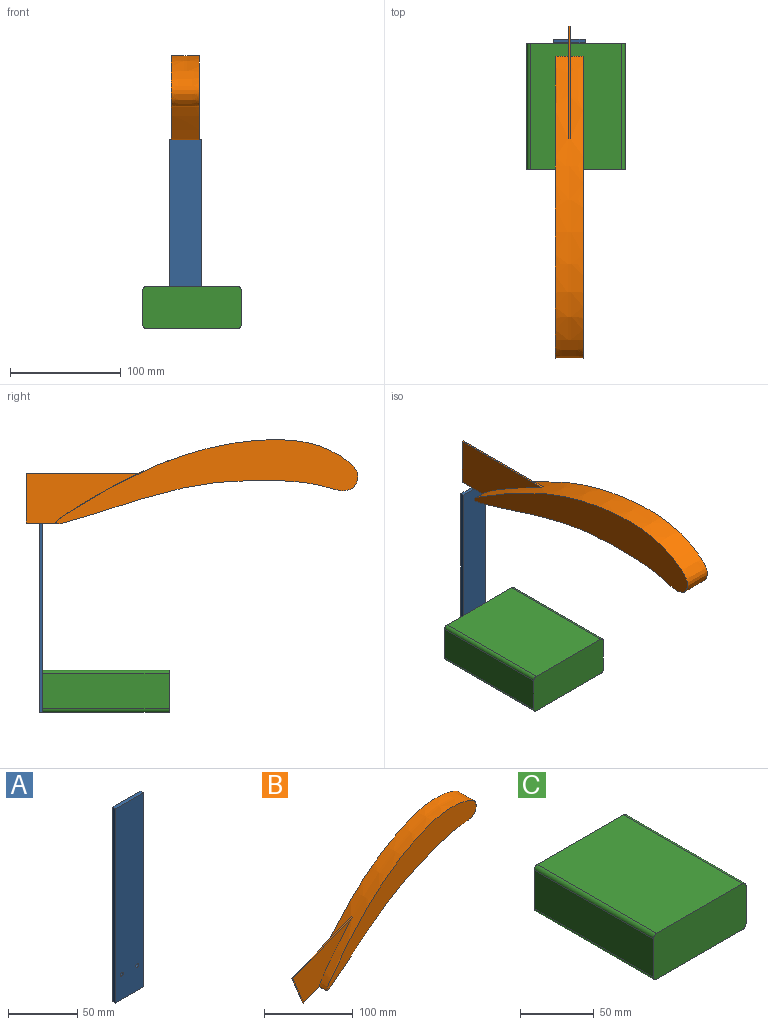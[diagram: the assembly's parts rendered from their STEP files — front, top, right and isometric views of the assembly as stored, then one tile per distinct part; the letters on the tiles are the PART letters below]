
ASSEMBLY  parts=3 mates=3
PART A: 8 faces, bbox 28.6x3.2x171.5 mm
  f0: plane 171.45x3.18mm, normal (1,0,0), area 544.4mm2, adj f1,f4,f6,f7
  f1: plane 28.58x3.18mm, normal (0,0,1), area 90.7mm2, adj f0,f2,f6,f7
  f2: plane 171.45x3.18mm, normal (-1,0,0), area 544.4mm2, adj f1,f4,f6,f7
  f3: cylinder r=1.59mm len=3.18mm, axis (0,-1,0), area 31.7mm2, adj f6,f7
  f4: plane 28.58x3.18mm, normal (0,0,-1), area 90.7mm2, adj f0,f2,f6,f7
  f5: cylinder r=1.59mm len=3.18mm, axis (0,-1,0), area 31.7mm2, adj f6,f7
  f6: plane 171.45x28.58mm, normal (0,1,0), area 4883.3mm2, adj f0,f1,f2,f3,f4,f5
  f7: plane 171.45x28.58mm, normal (0,-1,0), area 4883.3mm2, adj f0,f1,f2,f3,f4,f5
PART B: 8 faces, bbox 281x25.4x166.1 mm
  f0: extruded ~237.77x154.23mm, area 14786.6mm2, adj f1,f2,f3,f5,f6,f7
  f1: plane 241.53x156.81mm, normal (0,-1,0), area 7523.9mm2, adj f0
  f2: plane 241.53x156.81mm, normal (0,1,0), area 7523.9mm2, adj f0
  f3: plane 94.57x38.21mm, normal (-0.37,0,0.93), area 161.9mm2, adj f0,f4,f6,f7
  f4: plane 41.72x16.86mm, normal (-0.93,0,-0.37), area 71.4mm2, adj f3,f5,f6,f7
  f5: plane 25.19x10.18mm, normal (0.37,0,-0.93), area 43.1mm2, adj f0,f4,f6,f7
  f6: plane 96.16x81.52mm, normal (0,-1,0), area 2729.3mm2, adj f0,f3,f4,f5
  f7: plane 96.16x81.52mm, normal (0,1,0), area 2729.3mm2, adj f0,f3,f4,f5
PART C: 10 faces, bbox 88.9x114.3x38.1 mm
  f0: plane 114.3x31.75mm, normal (-1,0,0), area 3629mm2, adj f1,f7,f8,f9
  f1: cylinder r=3.17mm len=114.3mm, axis (0,1,0), area 570mm2, adj f0,f2,f8,f9
  f2: plane 114.3x82.55mm, normal (0,0,-1), area 9435.5mm2, adj f1,f3,f8,f9
  f3: cylinder r=3.17mm len=114.3mm, axis (0,1,0), area 570mm2, adj f2,f4,f8,f9
  f4: plane 114.3x31.75mm, normal (1,0,0), area 3629mm2, adj f3,f5,f8,f9
  f5: cylinder r=3.17mm len=114.3mm, axis (0,1,0), area 570mm2, adj f4,f6,f8,f9
  f6: plane 114.3x82.55mm, normal (0,0,1), area 9435.5mm2, adj f5,f7,f8,f9
  f7: cylinder r=3.17mm len=114.3mm, axis (0,1,0), area 570mm2, adj f0,f6,f8,f9
  f8: plane 88.9x38.1mm, normal (0,-1,0), area 3378.4mm2, adj f0,f1,f2,f3,f4,f5,f6,f7
  f9: plane 88.9x38.1mm, normal (0,1,0), area 3378.4mm2, adj f0,f1,f2,f3,f4,f5,f6,f7
PLACE A t=(-47.32,20.64,82.55)mm
PLACE B rot(axis=(0.19,0.19,-0.96),92.1deg) t=(-47.32,6.76,167.89)mm
PLACE C t=(-41.28,-38.1,15.88)mm fixed
MATE planar A.f7 <-> C.f9  axis (0,-1,0) through (-47.32,19.05,82.76)mm
MATE planar A.f1 <-> B.f5  axis (0,0,1) through (-47.32,20.64,168.28)mm
MATE planar A.f4 <-> C.f2  axis (0,0,-1) through (-47.32,20.64,-3.17)mm
